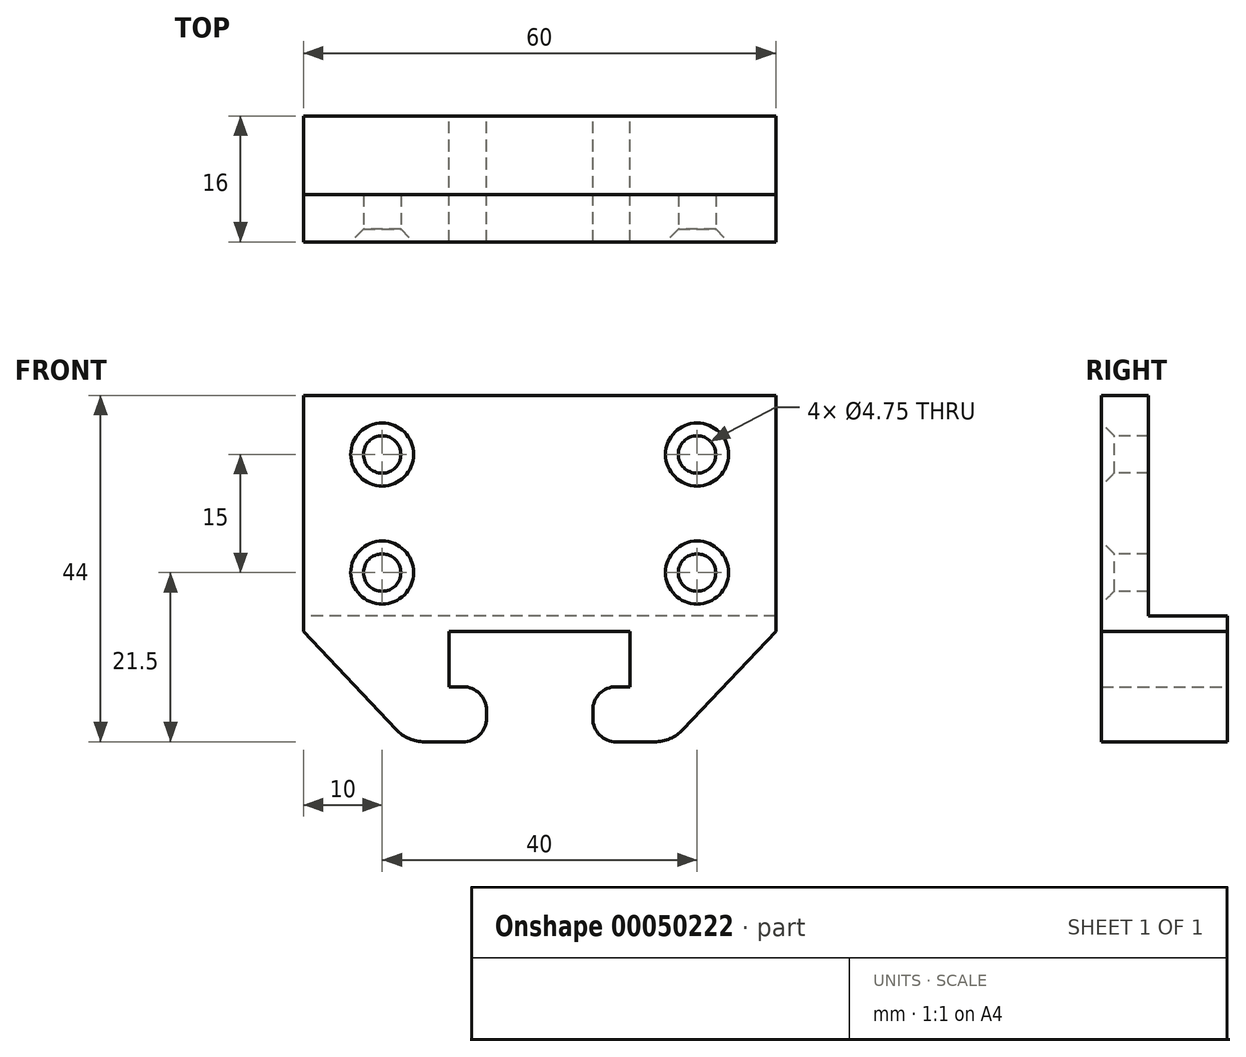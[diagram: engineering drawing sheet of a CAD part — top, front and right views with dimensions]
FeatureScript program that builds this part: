
annotation { "Feature Type Name" : "Feature", "Feature Type Description" : "" }
export const myFeature = defineFeature(function(context is Context, id is Id, definition is map)
    precondition{}
    {
        {
            var Q0;
            Q0=qCreatedBy(makeId("Front.planeOp"),FACE);
            var sketch = newSketch(context, id + "F0", { "sketchPlane" : qUnion([Q0])});
            skLineSegment(sketch, "E0", {"start": v(0, 0) * mm, "end": v(11.5, 0) * mm});
            skLineSegment(sketch, "E1", {"start": v(11.5, 0) * mm, "end": v(11.5, -7) * mm});
            skLineSegment(sketch, "E2", {"start": v(11.5, -7) * mm, "end": v(9.75, -7) * mm});
            skLineSegment(sketch, "E3", {"start": v(6.75, -10) * mm, "end": v(6.75, -11) * mm});
            skLineSegment(sketch, "E4", {"start": v(9.75, -14) * mm, "end": v(14.6, -14) * mm});
            skLineSegment(sketch, "E5", {"start": v(18.23, -12.44) * mm, "end": v(30, 0) * mm});
            skLineSegment(sketch, "E6", {"start": v(30, 0) * mm, "end": v(30, 30) * mm});
            skLineSegment(sketch, "E7", {"start": v(30, 30) * mm, "end": v(0, 30) * mm});
            skPoint(sketch, "E8.visualSharp", {"position": v(6.75, -7) * mm});
            skArc(sketch, "E8.filletArc", {"start": v(9.75, -7) * mm, "mid": v(7.63, -7.88) * mm, "end": v(6.75, -10) * mm});
            skPoint(sketch, "E9.visualSharp", {"position": v(6.75, -14) * mm});
            skArc(sketch, "E9.filletArc", {"start": v(6.75, -11) * mm, "mid": v(7.63, -13.12) * mm, "end": v(9.75, -14) * mm});
            skPoint(sketch, "E10.visualSharp", {"position": v(16.75, -14) * mm});
            skArc(sketch, "E10.filletArc", {"start": v(14.6, -14) * mm, "mid": v(16.57, -13.6) * mm, "end": v(18.23, -12.44) * mm});
            skLineSegment(sketch, "E11.MirrorCS", {"start": v(-6.75, -10) * mm, "end": v(-6.75, -11) * mm});
            skLineSegment(sketch, "E12.MirrorCS", {"start": v(-11.5, -7) * mm, "end": v(-9.75, -7) * mm});
            skArc(sketch, "E13.MirrorCS", {"start": v(-14.6, -14) * mm, "mid": v(-16.57, -13.6) * mm, "end": v(-18.23, -12.44) * mm});
            skLineSegment(sketch, "E14.MirrorCS", {"start": v(0, 0) * mm, "end": v(-11.5, 0) * mm});
            skPoint(sketch, "E15.MirrorP", {"position": v(-6.75, -7) * mm});
            skLineSegment(sketch, "E16.MirrorCS", {"start": v(-11.5, 0) * mm, "end": v(-11.5, -7) * mm});
            skPoint(sketch, "E17.MirrorP", {"position": v(-6.75, -14) * mm});
            skPoint(sketch, "E18.MirrorP", {"position": v(-16.75, -14) * mm});
            skArc(sketch, "E19.MirrorCS", {"start": v(-6.75, -11) * mm, "mid": v(-7.63, -13.12) * mm, "end": v(-9.75, -14) * mm});
            skArc(sketch, "E20.MirrorCS", {"start": v(-9.75, -7) * mm, "mid": v(-7.63, -7.88) * mm, "end": v(-6.75, -10) * mm});
            skLineSegment(sketch, "E21.MirrorCS", {"start": v(-30, 30) * mm, "end": v(0, 30) * mm});
            skLineSegment(sketch, "E22.MirrorCS", {"start": v(-30, 0) * mm, "end": v(-30, 30) * mm});
            skLineSegment(sketch, "E23.MirrorCS", {"start": v(-9.75, -14) * mm, "end": v(-14.6, -14) * mm});
            skLineSegment(sketch, "E24.MirrorCS", {"start": v(-18.23, -12.44) * mm, "end": v(-30, 0) * mm});
            skSolve(sketch);
        }
        {
            var Q0;
            Q0 = qSketchRegion(id + "F0", true);
            extrude(context, id + "F1", {"entities" : qUnion([Q0]), "depth" : 16 * mm});
        }
        {
            var Q0;
            Q0=qCreatedBy(makeId("Right.planeOp"),FACE);
            var sketch = newSketch(context, id + "F2", { "sketchPlane" : qUnion([Q0])});
            skLineSegment(sketch, "E25.bottom", {"start": v(10, 42) * mm, "end": v(-10, 42) * mm});
            skLineSegment(sketch, "E25.top", {"start": v(10, 2) * mm, "end": v(-10, 2) * mm});
            skLineSegment(sketch, "E25.left", {"start": v(10, 42) * mm, "end": v(10, 2) * mm});
            skLineSegment(sketch, "E25.right", {"start": v(-10, 42) * mm, "end": v(-10, 2) * mm});
            skSolve(sketch);
        }
        {
            var Q0;
            Q0 = qSketchRegion(id + "F2", true);
            extrude(context, id + "F3", {"entities" : qUnion([Q0]), "operationType" : NewBodyOperationType.REMOVE, "oppositeDirection" : true, "depth" : 100 * mm, "symmetric" : true});
        }
        {
            var Q0;
            Q0=makeQuery(id+"F1.opExtrude","CAP_FACE",FACE,{"disambiguationData":[OSD([sQuery(id+"F0.wireOp",EDGE,"E0"),sQuery(id+"F0.wireOp",EDGE,"E1"),sQuery(id+"F0.wireOp",EDGE,"E2"),sQuery(id+"F0.wireOp",EDGE,"E3"),sQuery(id+"F0.wireOp",EDGE,"E4"),sQuery(id+"F0.wireOp",EDGE,"E5"),sQuery(id+"F0.wireOp",EDGE,"E6"),sQuery(id+"F0.wireOp",EDGE,"E7"),sQuery(id+"F0.wireOp",EDGE,"E8.filletArc"),sQuery(id+"F0.wireOp",EDGE,"E9.filletArc"),sQuery(id+"F0.wireOp",EDGE,"E10.filletArc"),sQuery(id+"F0.wireOp",EDGE,"E11.MirrorCS"),sQuery(id+"F0.wireOp",EDGE,"E12.MirrorCS"),sQuery(id+"F0.wireOp",EDGE,"E13.MirrorCS"),sQuery(id+"F0.wireOp",EDGE,"E14.MirrorCS"),sQuery(id+"F0.wireOp",EDGE,"E16.MirrorCS"),sQuery(id+"F0.wireOp",EDGE,"E19.MirrorCS"),sQuery(id+"F0.wireOp",EDGE,"E20.MirrorCS"),sQuery(id+"F0.wireOp",EDGE,"E21.MirrorCS"),sQuery(id+"F0.wireOp",EDGE,"E22.MirrorCS"),sQuery(id+"F0.wireOp",EDGE,"E23.MirrorCS"),sQuery(id+"F0.wireOp",EDGE,"E24.MirrorCS")])],"isStart":false});
            var sketch = newSketch(context, id + "F4", { "sketchPlane" : qUnion([Q0])});
            skLineSegment(sketch, "E26", {"start": v(0, 22.5) * mm, "end": v(37.04, 22.5) * mm, "construction": true});
            skLineSegment(sketch, "E27", {"start": v(20, 28) * mm, "end": v(20, 0) * mm, "construction": true});
            skPoint(sketch, "E28", {"position": v(20, 22.5) * mm});
            skLineSegment(sketch, "E29", {"start": v(0, 15) * mm, "end": v(42.82, 15) * mm, "construction": true});
            skPoint(sketch, "E30.MirrorP", {"position": v(20, 7.5) * mm});
            skPoint(sketch, "E31.MirrorP", {"position": v(-20, 22.5) * mm});
            skPoint(sketch, "E32.MirrorP", {"position": v(-20, 7.5) * mm});
            skSolve(sketch);
        }
        {
            var Q0;
            Q0=sQuery(id+"F4.wireOp",VERTEX,"E28");
            var Q1;
            Q1=sQuery(id+"F4.wireOp",VERTEX,"E30.MirrorP");
            var Q2;
            Q2=sQuery(id+"F4.wireOp",VERTEX,"E31.MirrorP");
            var Q3;
            Q3=sQuery(id+"F4.wireOp",VERTEX,"E32.MirrorP");
            var Q4;
            Q4=makeQuery(id+"F1.opExtrude","SWEPT_BODY",BODY,{"disambiguationData":[OSD([sQuery(id+"F0.wireOp",EDGE,"E0"),sQuery(id+"F0.wireOp",EDGE,"E1"),sQuery(id+"F0.wireOp",EDGE,"E2"),sQuery(id+"F0.wireOp",EDGE,"E3"),sQuery(id+"F0.wireOp",EDGE,"E4"),sQuery(id+"F0.wireOp",EDGE,"E5"),sQuery(id+"F0.wireOp",EDGE,"E6"),sQuery(id+"F0.wireOp",EDGE,"E7"),sQuery(id+"F0.wireOp",EDGE,"E8.filletArc"),sQuery(id+"F0.wireOp",EDGE,"E9.filletArc"),sQuery(id+"F0.wireOp",EDGE,"E10.filletArc"),sQuery(id+"F0.wireOp",EDGE,"E11.MirrorCS"),sQuery(id+"F0.wireOp",EDGE,"E12.MirrorCS"),sQuery(id+"F0.wireOp",EDGE,"E13.MirrorCS"),sQuery(id+"F0.wireOp",EDGE,"E14.MirrorCS"),sQuery(id+"F0.wireOp",EDGE,"E16.MirrorCS"),sQuery(id+"F0.wireOp",EDGE,"E19.MirrorCS"),sQuery(id+"F0.wireOp",EDGE,"E20.MirrorCS"),sQuery(id+"F0.wireOp",EDGE,"E21.MirrorCS"),sQuery(id+"F0.wireOp",EDGE,"E22.MirrorCS"),sQuery(id+"F0.wireOp",EDGE,"E23.MirrorCS"),sQuery(id+"F0.wireOp",EDGE,"E24.MirrorCS")])]});
            hole(context, id + "F5", {"style" : HoleStyle.C_SINK, "holeDiameter" : 4.75 * mm, "cSinkDiameter" : 8 * mm, "endStyle" : HoleEndStyle.THROUGH, "locations" : qUnion([Q0, Q1, Q2, Q3]), "scope" : qUnion([Q4]), "cSinkAngle" : 90 * degree});
        }
    });
